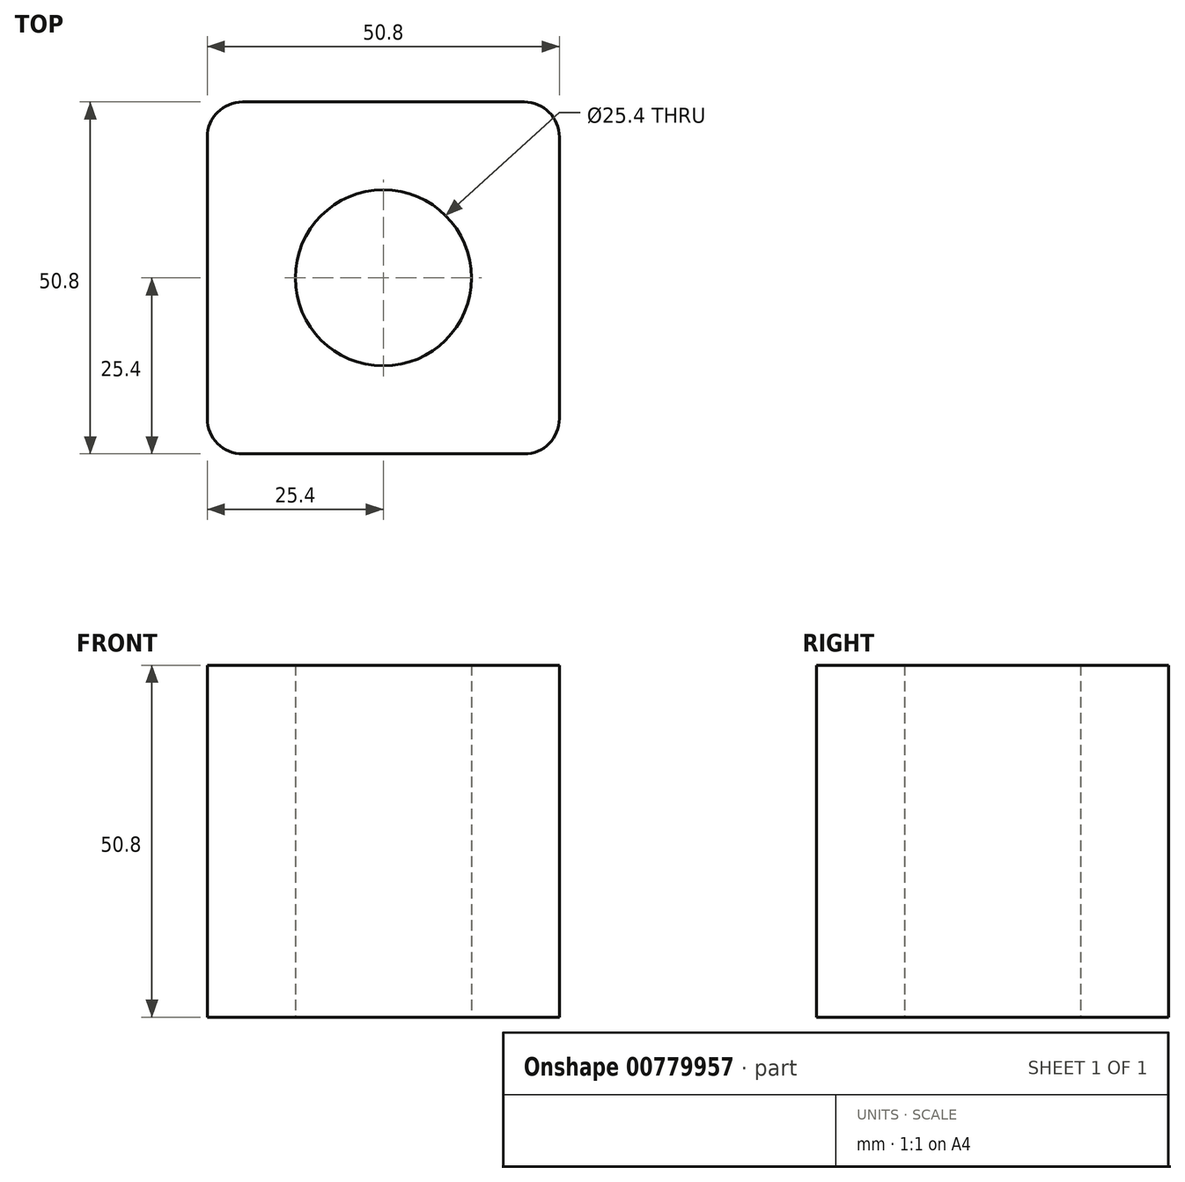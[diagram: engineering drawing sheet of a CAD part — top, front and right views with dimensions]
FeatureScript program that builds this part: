
annotation { "Feature Type Name" : "Feature", "Feature Type Description" : "" }
export const myFeature = defineFeature(function(context is Context, id is Id, definition is map)
    precondition{}
    {
        {
            var Q0;
            Q0=qCreatedBy(makeId("Top.planeOp"),FACE);
            var sketch = newSketch(context, id + "F0", { "sketchPlane" : qUnion([Q0])});
            skLineSegment(sketch, "E0.bottom", {"start": v(25.4, -25.4) * mm, "end": v(-25.4, -25.4) * mm});
            skLineSegment(sketch, "E0.top", {"start": v(25.4, 25.4) * mm, "end": v(-25.4, 25.4) * mm});
            skLineSegment(sketch, "E0.left", {"start": v(25.4, -25.4) * mm, "end": v(25.4, 25.4) * mm});
            skLineSegment(sketch, "E0.right", {"start": v(-25.4, -25.4) * mm, "end": v(-25.4, 25.4) * mm});
            skPoint(sketch, "E0.middle", {"position": v(0, 0) * mm});
            skCircle(sketch, "E1", {"center": v(0, 0) * mm, "radius": 12.7 * mm});
            skSolve(sketch);
        }
        {
            var Q0;
            Q0=makeQuery(id+"F0.imprint","IMPRINT",FACE,{"disambiguationData":[TD([[makeQuery(id+"F0.imprint","IMPRINT",EDGE,{"derivedFrom":sQuery(id+"F0.wireOp",EDGE,"E0.bottom")}),-1.0]])]});
            extrude(context, id + "F1", {"entities" : qUnion([Q0]), "depth" : 50.8 * mm, "offsetDistance" : 25.4 * mm});
        }
        {
            var Q0;
            Q0=makeQuery(id+"F1.opExtrude","SWEPT_EDGE",EDGE,{"disambiguationData":[OSD([sQuery(id+"F0.wireOp",EDGE,"E0.top"),sQuery(id+"F0.wireOp",EDGE,"E0.left")])]});
            var Q1;
            Q1=makeQuery(id+"F1.opExtrude","SWEPT_EDGE",EDGE,{"disambiguationData":[OSD([sQuery(id+"F0.wireOp",EDGE,"E0.top"),sQuery(id+"F0.wireOp",EDGE,"E0.right")])]});
            var Q2;
            Q2=makeQuery(id+"F1.opExtrude","SWEPT_EDGE",EDGE,{"disambiguationData":[OSD([sQuery(id+"F0.wireOp",EDGE,"E0.bottom"),sQuery(id+"F0.wireOp",EDGE,"E0.left")])]});
            var Q3;
            Q3=makeQuery(id+"F1.opExtrude","SWEPT_EDGE",EDGE,{"disambiguationData":[OSD([sQuery(id+"F0.wireOp",EDGE,"E0.bottom"),sQuery(id+"F0.wireOp",EDGE,"E0.right")])]});
            fillet(context, id + "F2", {"entities" : qUnion([Q0, Q1, Q2, Q3]), "radius" : 5.08 * mm, "tangentPropagation" : true, "allowEdgeOverflow" : false});
        }
    });
